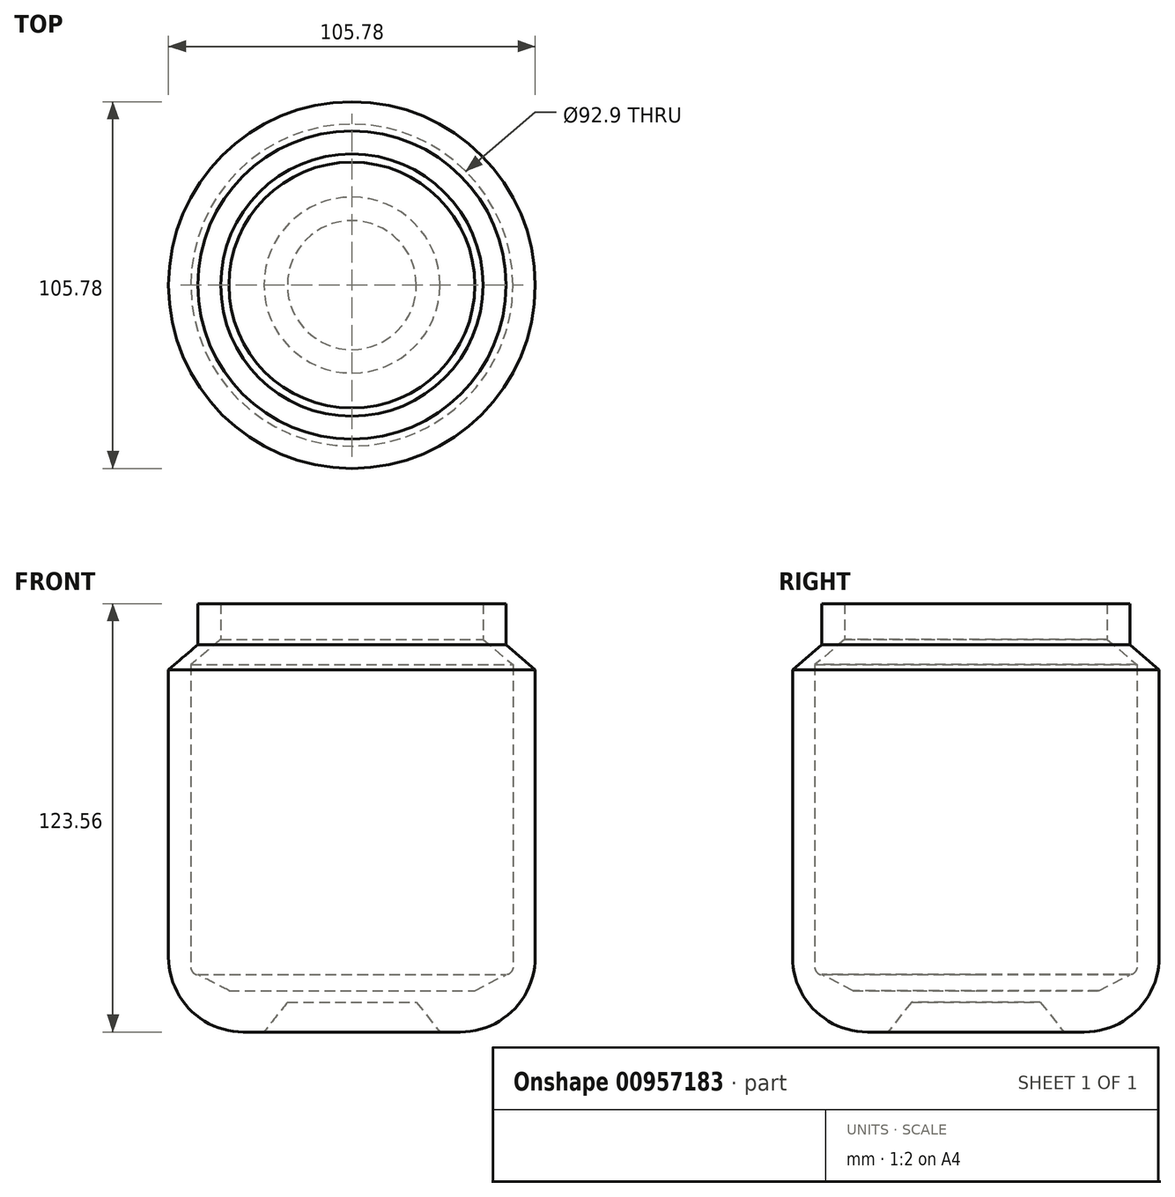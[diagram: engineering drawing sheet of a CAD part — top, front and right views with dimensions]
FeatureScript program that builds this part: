
annotation { "Feature Type Name" : "Feature", "Feature Type Description" : "" }
export const myFeature = defineFeature(function(context is Context, id is Id, definition is map)
    precondition{}
    {
        {
            var Q0;
            Q0=qCreatedBy(makeId("Front.planeOp"),FACE);
            var sketch = newSketch(context, id + "F0", { "sketchPlane" : qUnion([Q0])});
            skLineSegment(sketch, "E0", {"start": v(0, 0) * mm, "end": v(0, 74.82) * mm, "construction": true});
            skLineSegment(sketch, "E1", {"start": v(0, 0) * mm, "end": v(18.59, 0) * mm});
            skLineSegment(sketch, "E2", {"start": v(18.59, 0) * mm, "end": v(25.38, -8.59) * mm});
            skLineSegment(sketch, "E3", {"start": v(25.38, -8.59) * mm, "end": v(31.3, -8.59) * mm});
            skLineSegment(sketch, "E4", {"start": v(52.89, 13) * mm, "end": v(52.89, 95.92) * mm});
            skLineSegment(sketch, "E5", {"start": v(52.89, 95.92) * mm, "end": v(44.44, 103.14) * mm});
            skLineSegment(sketch, "E6", {"start": v(44.44, 103.14) * mm, "end": v(44.44, 114.97) * mm});
            skLineSegment(sketch, "E7", {"start": v(44.44, 114.97) * mm, "end": v(37.83, 114.97) * mm});
            skLineSegment(sketch, "E8", {"start": v(37.83, 114.97) * mm, "end": v(37.83, 104.65) * mm});
            skLineSegment(sketch, "E9", {"start": v(37.83, 104.65) * mm, "end": v(46.45, 97.34) * mm});
            skLineSegment(sketch, "E10", {"start": v(46.45, 97.34) * mm, "end": v(46.45, 10.06) * mm});
            skLineSegment(sketch, "E11", {"start": v(44.44, 7.94) * mm, "end": v(44.33, 7.94) * mm});
            skLineSegment(sketch, "E12", {"start": v(44.44, 7.94) * mm, "end": v(35.46, 3.36) * mm});
            skLineSegment(sketch, "E13", {"start": v(35.46, 3.36) * mm, "end": v(0, 3.36) * mm});
            skLineSegment(sketch, "E14", {"start": v(0, 3.36) * mm, "end": v(0, 0) * mm});
            skPoint(sketch, "E15.visualSharp", {"position": v(52.89, -8.59) * mm});
            skArc(sketch, "E15.filletArc", {"start": v(31.3, -8.59) * mm, "mid": v(46.56, -2.26) * mm, "end": v(52.89, 13) * mm});
            skPoint(sketch, "E16.visualSharp", {"position": v(46.45, 7.94) * mm});
            skArc(sketch, "E16.filletArc", {"start": v(44.33, 7.94) * mm, "mid": v(45.83, 8.56) * mm, "end": v(46.45, 10.06) * mm});
            skSolve(sketch);
        }
        {
            var Q0;
            Q0 = qSketchRegion(id + "F0", true);
            var Q1;
            Q1=sQuery(id+"F0.wireOp",EDGE,"E0");
            revolve(context, id + "F1", {"surfaceOperationType" : NewSurfaceOperationType.NEW, "entities" : qUnion([Q0]), "axis" : qUnion([Q1]), "revolveType" : RevolveType.FULL});
        }
    });
